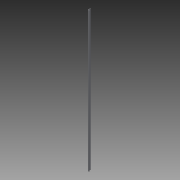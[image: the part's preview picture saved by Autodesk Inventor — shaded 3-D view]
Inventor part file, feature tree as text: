
AUTODESK INVENTOR PART (.ipt)
format: ipt  version: 2015 SP1 (Build 190203100, 203)  size: 77,312 bytes
history: native  units: mm
features: extrude x1, sketch x1
ambient origin geometry x8: Origin, YZ Plane, XZ Plane, XY Plane, X Axis, Y Axis, Z Axis, Center Point
bodies: Solid1 (feature_tree)
feature tree (2):
  extrude  "Extrusion1"  Depth=4.0mm
  sketch  "Sketch1"  dims[d1=40.0mm d2=4.0mm d3=20.0mm d4=4.0mm d5=4.0mm d6=2000.0mm d7=0.0mm]
